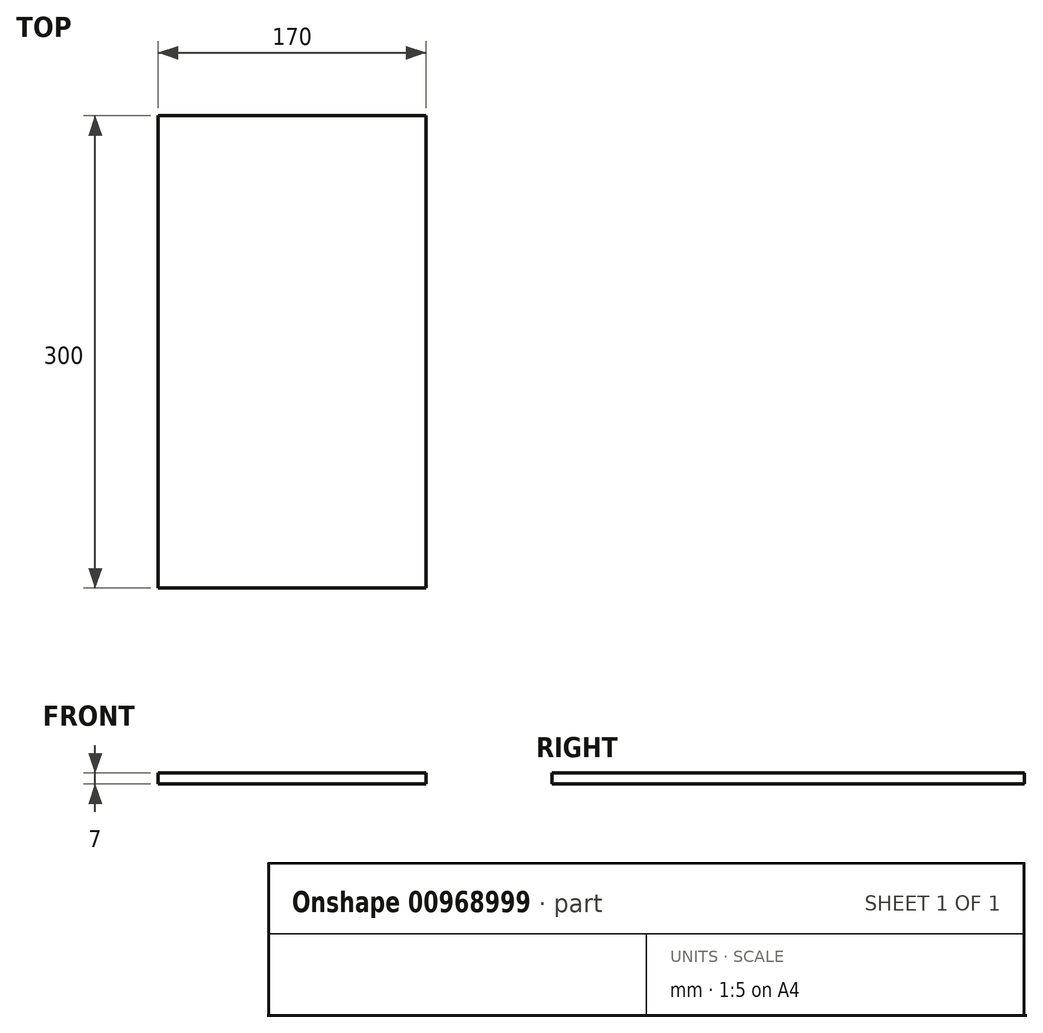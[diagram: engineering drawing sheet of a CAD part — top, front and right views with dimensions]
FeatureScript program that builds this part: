
annotation { "Feature Type Name" : "Feature", "Feature Type Description" : "" }
export const myFeature = defineFeature(function(context is Context, id is Id, definition is map)
    precondition{}
    {
        {
            var Q0;
            Q0=qCreatedBy(makeId("Top.planeOp"),FACE);
            var sketch = newSketch(context, id + "F0", { "sketchPlane" : qUnion([Q0])});
            skLineSegment(sketch, "E0.bottom", {"start": v(85, 150) * mm, "end": v(-85, 150) * mm});
            skLineSegment(sketch, "E0.top", {"start": v(85, -150) * mm, "end": v(-85, -150) * mm});
            skLineSegment(sketch, "E0.left", {"start": v(85, 150) * mm, "end": v(85, -150) * mm});
            skLineSegment(sketch, "E0.right", {"start": v(-85, 150) * mm, "end": v(-85, -150) * mm});
            skPoint(sketch, "E0.middle", {"position": v(0, 0) * mm});
            skSolve(sketch);
        }
        {
            var Q0;
            Q0=makeQuery(id+"F0.imprint","IMPRINT",FACE,{"disambiguationData":[TD([[makeQuery(id+"F0.imprint","IMPRINT",EDGE,{"derivedFrom":sQuery(id+"F0.wireOp",EDGE,"E0.bottom")}),1.0]])]});
            extrude(context, id + "F1", {"entities" : qUnion([Q0]), "depth" : 7 * mm, "offsetDistance" : 25 * mm});
        }
    });
